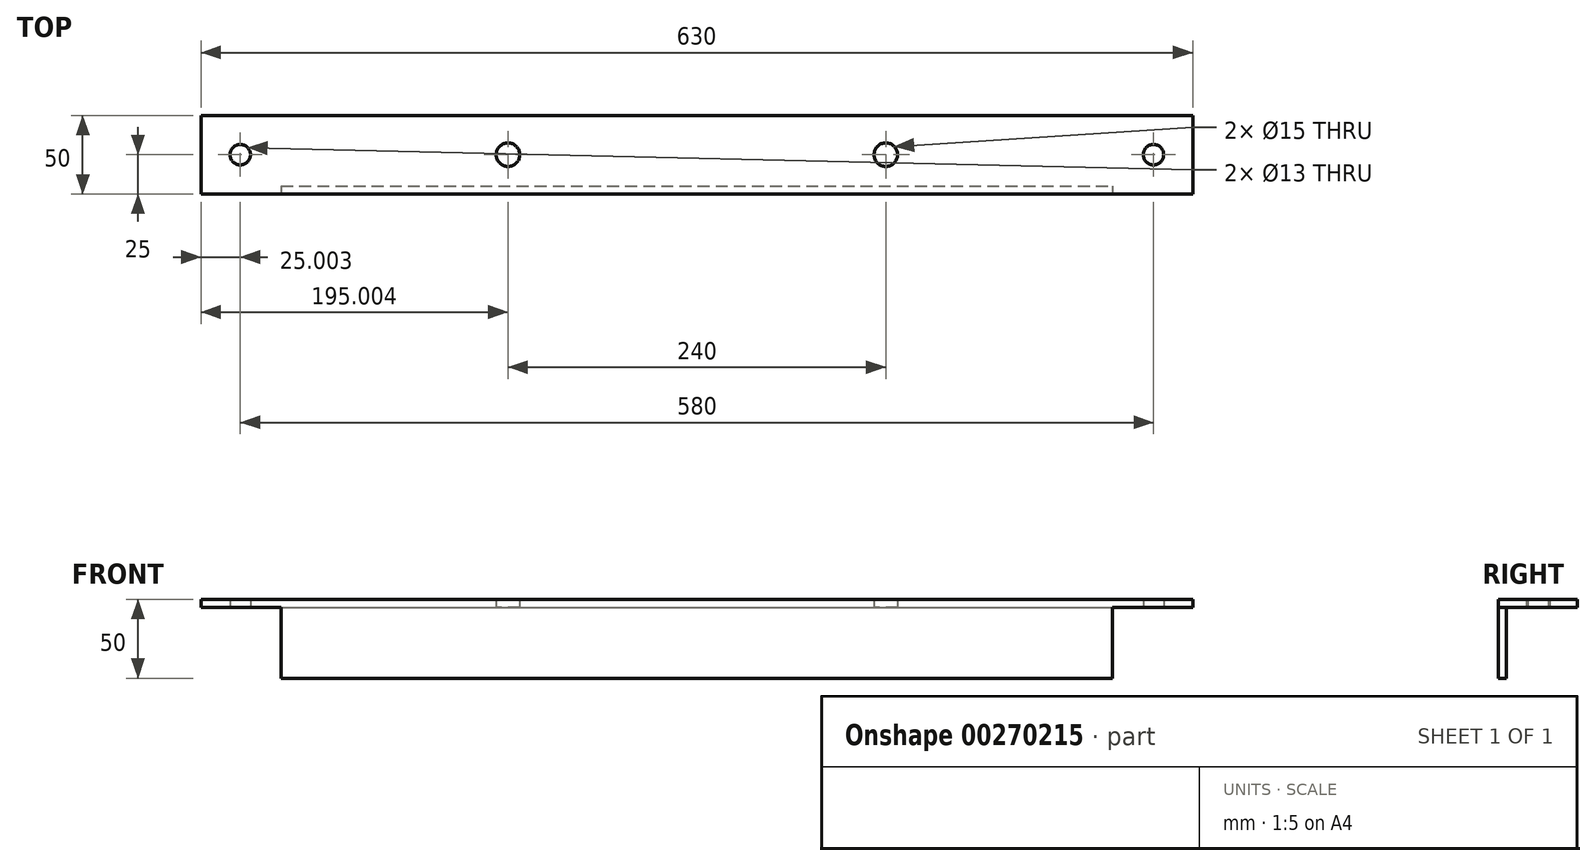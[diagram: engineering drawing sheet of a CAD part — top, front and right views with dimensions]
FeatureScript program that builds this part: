
annotation { "Feature Type Name" : "Feature", "Feature Type Description" : "" }
export const myFeature = defineFeature(function(context is Context, id is Id, definition is map)
    precondition{}
    {
        {
            var Q0;
            Q0=qCreatedBy(makeId("Top.planeOp"),FACE);
            var sketch = newSketch(context, id + "F0", { "sketchPlane" : qUnion([Q0])});
            skLineSegment(sketch, "E0", {"start": v(-332, 25) * mm, "end": v(298, 25) * mm});
            skLineSegment(sketch, "E1", {"start": v(-332, 25) * mm, "end": v(-332, -25) * mm});
            skLineSegment(sketch, "E2", {"start": v(-332, -25) * mm, "end": v(-281, -25) * mm});
            skLineSegment(sketch, "E3", {"start": v(298, 25) * mm, "end": v(298, -25) * mm});
            skLineSegment(sketch, "E4", {"start": v(298, -25) * mm, "end": v(247, -25) * mm});
            skLineSegment(sketch, "E5", {"start": v(-281, -25) * mm, "end": v(247, -25) * mm});
            skCircle(sketch, "E6", {"center": v(-307, 0) * mm, "radius": 6.5 * mm});
            skCircle(sketch, "E7", {"center": v(273, 0) * mm, "radius": 6.5 * mm});
            skCircle(sketch, "E8", {"center": v(-137, 0) * mm, "radius": 7.5 * mm});
            skCircle(sketch, "E9", {"center": v(103, 0) * mm, "radius": 7.5 * mm});
            skSolve(sketch);
        }
        {
            var Q0;
            Q0=makeQuery(id+"F0.imprint","IMPRINT",FACE,{"disambiguationData":[TD([[makeQuery(id+"F0.imprint","IMPRINT",EDGE,{"derivedFrom":sQuery(id+"F0.wireOp",EDGE,"E0")}),-1.0]])]});
            extrude(context, id + "F1", {"entities" : qUnion([Q0]), "depth" : 5 * mm});
        }
        {
            var Q0;
            Q0=makeQuery(id+"F1.opExtrude","SWEPT_FACE",FACE,{"disambiguationData":[OSD([sQuery(id+"F0.wireOp",EDGE,"E2"),sQuery(id+"F0.wireOp",EDGE,"E4"),sQuery(id+"F0.wireOp",EDGE,"E5")])]});
            var sketch = newSketch(context, id + "F2", { "sketchPlane" : qUnion([Q0])});
            skLineSegment(sketch, "E10", {"start": v(-281, 0) * mm, "end": v(-281, -45) * mm});
            skLineSegment(sketch, "E11", {"start": v(-281, -45) * mm, "end": v(247, -45) * mm});
            skLineSegment(sketch, "E12", {"start": v(247, -45) * mm, "end": v(247, 0) * mm});
            skSolve(sketch);
        }
        {
            var Q0;
            {var subQ0=sQuery(id+"F2.wireOp",EDGE,"E10");Q0=makeQuery(id+"F2.imprint","IMPRINT",FACE,{"disambiguationData":[TD([[makeQuery(id+"F2.imprint","IMPRINT",EDGE,{"derivedFrom":subQ0}),1.0]])]});}
            extrude(context, id + "F3", {"entities" : qUnion([Q0]), "operationType" : NewBodyOperationType.ADD, "oppositeDirection" : true, "depth" : 5 * mm});
        }
    });
